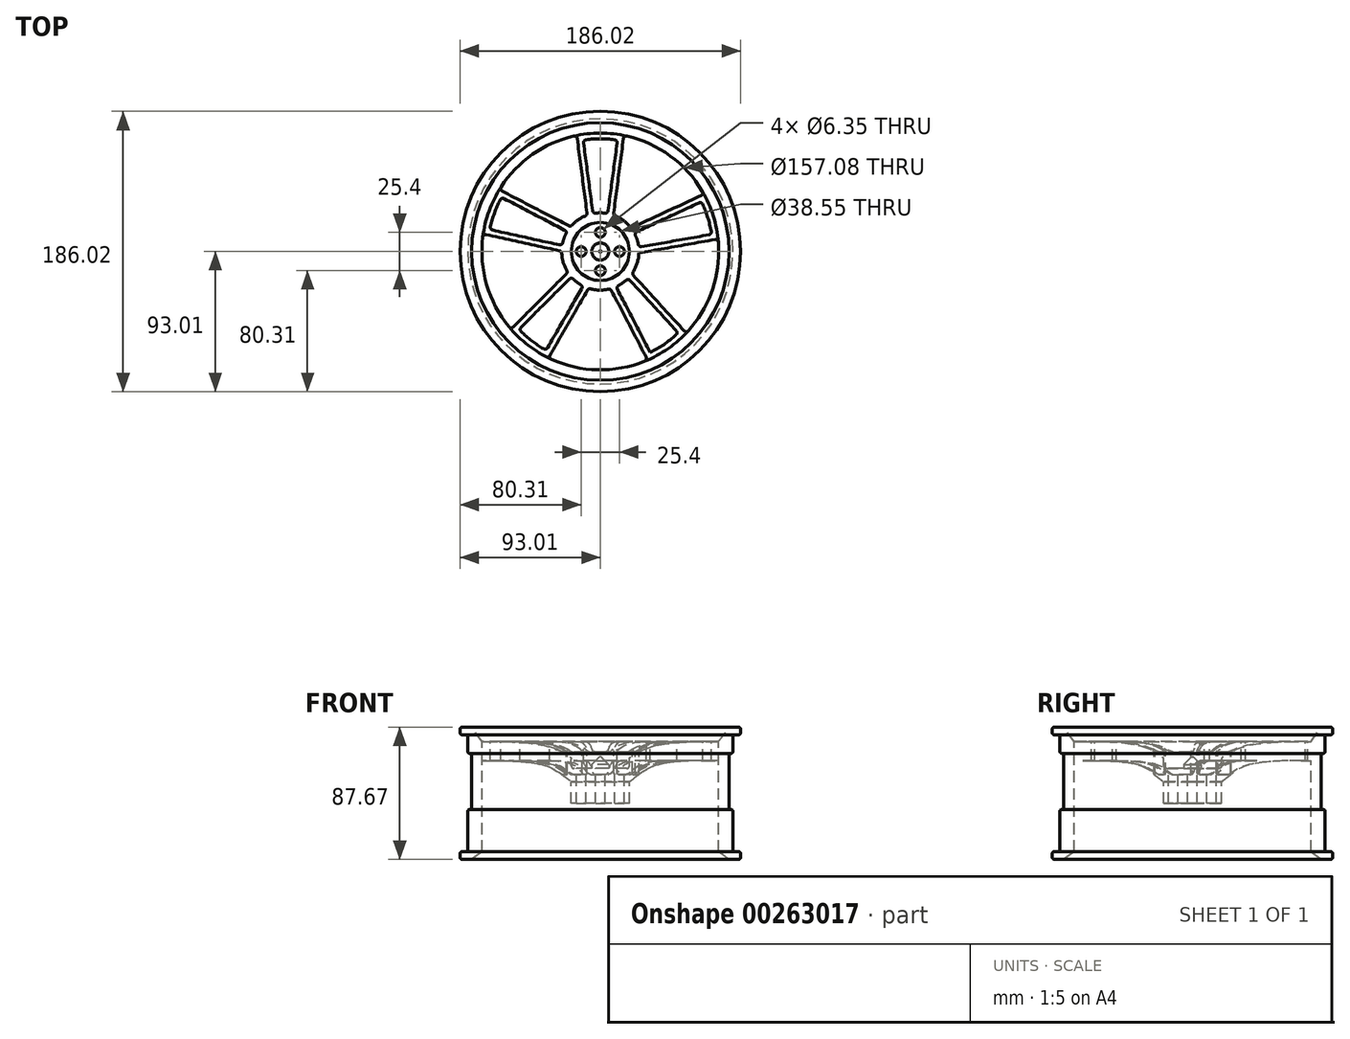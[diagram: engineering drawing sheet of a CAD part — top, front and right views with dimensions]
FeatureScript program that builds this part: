
annotation { "Feature Type Name" : "Feature", "Feature Type Description" : "" }
export const myFeature = defineFeature(function(context is Context, id is Id, definition is map)
    precondition{}
    {
        {
            var Q0;
            Q0=qCreatedBy(makeId("Front.planeOp"),FACE);
            var sketch = newSketch(context, id + "F0", { "sketchPlane" : qUnion([Q0])});
            skLineSegment(sketch, "E0", {"start": v(0, 54) * mm, "end": v(0, -73) * mm, "construction": true});
            skLineSegment(sketch, "E1", {"start": v(-93, 40.83) * mm, "end": v(-85.39, 40.83) * mm});
            skLineSegment(sketch, "E2", {"start": v(-85.39, 40.83) * mm, "end": v(-78.54, 31.34) * mm});
            skLineSegment(sketch, "E3", {"start": v(-78.54, 18.64) * mm, "end": v(-78.54, -41.76) * mm});
            skLineSegment(sketch, "E4", {"start": v(-78.54, -41.76) * mm, "end": v(-85.39, -46.84) * mm});
            skLineSegment(sketch, "E5", {"start": v(-85.39, -46.84) * mm, "end": v(-93, -46.84) * mm});
            skLineSegment(sketch, "E6", {"start": v(-93, -46.84) * mm, "end": v(-93, -41.76) * mm});
            skLineSegment(sketch, "E7", {"start": v(-93, -41.76) * mm, "end": v(-87.93, -41.76) * mm});
            skLineSegment(sketch, "E8", {"start": v(-87.93, -41.76) * mm, "end": v(-87.93, -13.7) * mm});
            skLineSegment(sketch, "E9", {"start": v(-87.93, -13.7) * mm, "end": v(-85.39, -13.7) * mm});
            skLineSegment(sketch, "E10", {"start": v(-85.39, -13.7) * mm, "end": v(-85.39, 23.42) * mm});
            skLineSegment(sketch, "E11", {"start": v(-85.39, 23.42) * mm, "end": v(-87.93, 23.42) * mm});
            skLineSegment(sketch, "E12", {"start": v(-87.93, 23.42) * mm, "end": v(-87.93, 35.75) * mm});
            skLineSegment(sketch, "E13", {"start": v(-87.93, 35.75) * mm, "end": v(-93, 35.75) * mm});
            skLineSegment(sketch, "E14", {"start": v(-93, 40.83) * mm, "end": v(-93, 35.75) * mm});
            skFitSpline(sketch, "E15", {"points": [v(-78.54, 31.34) * mm, v(-32.5, 27.25) * mm, v(-11.3, 14.38) * mm], "startDerivative": vector(88.3, -0.35) * mm, "endDerivative": vector(43.9, -35.39) * mm});
            skFitSpline(sketch, "E16.0", {"points": [v(-78.6, 18.65) * mm, v(-74.91, 18.63) * mm, v(-69.46, 18.6) * mm, v(-62.5, 18.47) * mm, v(-57.46, 18.27) * mm, v(-52.66, 17.98) * mm, v(-48.17, 17.55) * mm, v(-44.03, 16.99) * mm, v(-40.92, 16.4) * mm, v(-38.68, 15.85) * mm, v(-37.13, 15.4) * mm, v(-35.72, 14.94) * mm, v(-34.36, 14.43) * mm, v(-33.06, 13.87) * mm, v(-31.38, 13.06) * mm, v(-29.34, 11.93) * mm, v(-26.93, 10.37) * mm, v(-23.67, 8.03) * mm, v(-21.1, 5.96) * mm, v(-19.27, 4.5) * mm]});
            skLineSegment(sketch, "E17", {"start": v(-19.27, 4.5) * mm, "end": v(-19.27, -9.86) * mm});
            skLineSegment(sketch, "E18", {"start": v(-19.27, -9.86) * mm, "end": v(0, -9.86) * mm});
            skLineSegment(sketch, "E19", {"start": v(0, -9.86) * mm, "end": v(0, 13.32) * mm});
            skLineSegment(sketch, "E20", {"start": v(0, 13.32) * mm, "end": v(-19.27, 13.32) * mm});
            skLineSegment(sketch, "E21", {"start": v(-19.27, 13.32) * mm, "end": v(-19.27, 20.5) * mm});
            skSolve(sketch);
        }
        {
            var Q0;
            Q0=makeQuery(id+"F0.imprint","IMPRINT",FACE,{"disambiguationData":[TD([[makeQuery(id+"F0.imprint","IMPRINT",EDGE,{"derivedFrom":sQuery(id+"F0.wireOp",EDGE,"E1")}),-1.0]])]});
            var Q1;
            Q1=sQuery(id+"F0.wireOp",EDGE,"E0");
            revolve(context, id + "F1", {"entities" : qUnion([Q0]), "axis" : qUnion([Q1]), "revolveType" : RevolveType.FULL});
        }
        {
            var Q0;
            Q0=makeQuery(id+"F1.opRevolve","SWEPT_FACE",FACE,{"disambiguationData":[OSD([sQuery(id+"F0.wireOp",EDGE,"E1")])]});
            var sketch = newSketch(context, id + "F2", { "sketchPlane" : qUnion([Q0])});
            skArc(sketch, "E22.0", {"start": v(-77.67, 11.66) * mm, "mid": v(-75.4, -21.98) * mm, "end": v(-59.24, -51.57) * mm});
            skCircle(sketch, "E23.0", {"center": v(0, 0) * mm, "radius": 19.27 * mm});
            skArc(sketch, "E24.0", {"start": v(-25.62, 0.12) * mm, "mid": v(-24.6, -7.17) * mm, "end": v(-21.54, -13.87) * mm});
            skLineSegment(sketch, "E25", {"start": v(-8.65, 24.12) * mm, "end": v(-15.6, 76.98) * mm});
            skLineSegment(sketch, "E26", {"start": v(0, 78.54) * mm, "end": v(0, 0) * mm, "construction": true});
            skLineSegment(sketch, "E27.MirrorCS", {"start": v(8.65, 24.12) * mm, "end": v(15.6, 76.98) * mm});
            skLineSegment(sketch, "E28.1.0", {"start": v(25.6, -1) * mm, "end": v(78.1, 8.26) * mm});
            skLineSegment(sketch, "E28.1.1", {"start": v(20.4, 15.5) * mm, "end": v(68.72, 38.03) * mm});
            skLineSegment(sketch, "E28.2.0", {"start": v(6.75, -24.72) * mm, "end": v(31.37, -72) * mm});
            skLineSegment(sketch, "E28.2.1", {"start": v(20.92, -14.8) * mm, "end": v(56.93, -54.1) * mm});
            skLineSegment(sketch, "E28.3.0", {"start": v(-21.54, -13.87) * mm, "end": v(-59.24, -51.57) * mm});
            skLineSegment(sketch, "E28.3.1", {"start": v(-7.82, -24.4) * mm, "end": v(-34.48, -70.57) * mm});
            skLineSegment(sketch, "E28.4.0", {"start": v(-19.7, 16.37) * mm, "end": v(-67, 41) * mm});
            skLineSegment(sketch, "E28.4.1", {"start": v(-25.62, 0.12) * mm, "end": v(-77.67, 11.66) * mm});
            skLineSegment(sketch, "E28.anchor1", {"start": v(0, 0) * mm, "end": v(8.65, 24.12) * mm, "construction": true});
            skLineSegment(sketch, "E28.anchor2", {"start": v(0, 0) * mm, "end": v(-19.7, 16.37) * mm, "construction": true});
            skArc(sketch, "E29.trimOffspring", {"start": v(-8.65, 24.12) * mm, "mid": v(-14.7, 20.99) * mm, "end": v(-19.7, 16.37) * mm});
            skArc(sketch, "E30.trimOffspring", {"start": v(-15.6, 76.98) * mm, "mid": v(-45.05, 64.34) * mm, "end": v(-67, 41) * mm});
            skArc(sketch, "E31.trimOffspring", {"start": v(20.4, 15.5) * mm, "mid": v(15.15, 20.66) * mm, "end": v(8.65, 24.12) * mm});
            skArc(sketch, "E32.trimOffspring", {"start": v(68.72, 38.03) * mm, "mid": v(46.44, 63.34) * mm, "end": v(15.6, 76.98) * mm});
            skArc(sketch, "E33.trimOffspring", {"start": v(56.93, -54.1) * mm, "mid": v(74.37, -25.25) * mm, "end": v(78.1, 8.26) * mm});
            skArc(sketch, "E34.trimOffspring", {"start": v(20.92, -14.8) * mm, "mid": v(24.26, -8.24) * mm, "end": v(25.6, -1) * mm});
            skArc(sketch, "E35.trimOffspring", {"start": v(-7.82, -24.4) * mm, "mid": v(-0.56, -25.62) * mm, "end": v(6.75, -24.72) * mm});
            skArc(sketch, "E36.trimOffspring", {"start": v(-34.48, -70.57) * mm, "mid": v(-1.71, -78.52) * mm, "end": v(31.37, -72) * mm});
            skSolve(sketch);
        }
        {
            var Q0;
            Q0=makeQuery(id+"F1.opRevolve","SWEPT_EDGE",EDGE,{"disambiguationData":[OSD([sQuery(id+"F0.wireOp",EDGE,"E6"),sQuery(id+"F0.wireOp",EDGE,"E7")])]});
            var Q1;
            Q1=makeQuery(id+"F1.opRevolve","SWEPT_FACE",FACE,{"disambiguationData":[OSD([sQuery(id+"F0.wireOp",EDGE,"E10")])]});
            var Q2;
            Q2=makeQuery(id+"F1.opRevolve","SWEPT_EDGE",EDGE,{"disambiguationData":[OSD([sQuery(id+"F0.wireOp",EDGE,"E8"),sQuery(id+"F0.wireOp",EDGE,"E9")])]});
            var Q3;
            Q3=makeQuery(id+"F1.opRevolve","SWEPT_EDGE",EDGE,{"disambiguationData":[OSD([sQuery(id+"F0.wireOp",EDGE,"E11"),sQuery(id+"F0.wireOp",EDGE,"E12")])]});
            var Q4;
            Q4=makeQuery(id+"F1.opRevolve","SWEPT_EDGE",EDGE,{"disambiguationData":[OSD([sQuery(id+"F0.wireOp",EDGE,"E13"),sQuery(id+"F0.wireOp",EDGE,"E14")])]});
            var Q5;
            Q5=makeQuery(id+"F1.opRevolve","SWEPT_EDGE",EDGE,{"disambiguationData":[OSD([sQuery(id+"F0.wireOp",EDGE,"E12"),sQuery(id+"F0.wireOp",EDGE,"E13")])]});
            var Q6;
            Q6=makeQuery(id+"F1.opRevolve","SWEPT_EDGE",EDGE,{"disambiguationData":[OSD([sQuery(id+"F0.wireOp",EDGE,"E1"),sQuery(id+"F0.wireOp",EDGE,"E14")])]});
            var Q7;
            Q7=makeQuery(id+"F1.opRevolve","SWEPT_EDGE",EDGE,{"disambiguationData":[OSD([sQuery(id+"F0.wireOp",EDGE,"E5"),sQuery(id+"F0.wireOp",EDGE,"E6")])]});
            fillet(context, id + "F3", {"entities" : qUnion([Q0, Q1, Q2, Q3, Q4, Q5, Q6, Q7]), "radius" : 1.27 * mm, "tangentPropagation" : true, "allowEdgeOverflow" : false});
        }
        {
            var Q0;
            Q0=makeQuery(id+"F2.imprint","IMPRINT",FACE,{"disambiguationData":[TD([[makeQuery(id+"F2.imprint","IMPRINT",EDGE,{"derivedFrom":sQuery(id+"F2.wireOp",EDGE,"E28.1.0")}),-1.0]])]});
            var Q1;
            Q1=makeQuery(id+"F2.imprint","IMPRINT",FACE,{"disambiguationData":[TD([[makeQuery(id+"F2.imprint","IMPRINT",EDGE,{"derivedFrom":sQuery(id+"F2.wireOp",EDGE,"E27.MirrorCS")}),-1.0]])]});
            var Q2;
            Q2=makeQuery(id+"F2.imprint","IMPRINT",FACE,{"disambiguationData":[TD([[makeQuery(id+"F2.imprint","IMPRINT",EDGE,{"derivedFrom":sQuery(id+"F2.wireOp",EDGE,"E25")}),1.0]])]});
            var Q3;
            Q3=makeQuery(id+"F2.imprint","IMPRINT",FACE,{"disambiguationData":[TD([[makeQuery(id+"F2.imprint","IMPRINT",EDGE,{"derivedFrom":sQuery(id+"F2.wireOp",EDGE,"E22.0")}),1.0]])]});
            var Q4;
            Q4=makeQuery(id+"F2.imprint","IMPRINT",FACE,{"disambiguationData":[TD([[makeQuery(id+"F2.imprint","IMPRINT",EDGE,{"derivedFrom":sQuery(id+"F2.wireOp",EDGE,"E28.2.0")}),-1.0]])]});
            extrude(context, id + "F4", {"entities" : qUnion([Q0, Q1, Q2, Q3, Q4]), "operationType" : NewBodyOperationType.REMOVE, "oppositeDirection" : true, "depth" : 127 * mm});
        }
        {
            var Q0;
            Q0=makeQuery(id+"F1.opRevolve","SWEPT_FACE",FACE,{"disambiguationData":[OSD([sQuery(id+"F0.wireOp",EDGE,"E1")])]});
            var sketch = newSketch(context, id + "F5", { "sketchPlane" : qUnion([Q0])});
            skArc(sketch, "E37.0", {"start": v(11.35, 73.87) * mm, "mid": v(0, 74.73) * mm, "end": v(-11.35, 73.87) * mm});
            skPoint(sketch, "E38.2.end.orphan", {"position": v(8.65, 24.12) * mm});
            skPoint(sketch, "E38.2.start.orphan", {"position": v(15.6, 76.98) * mm});
            skPoint(sketch, "E38.1.end.orphan", {"position": v(-8.65, 24.12) * mm});
            skPoint(sketch, "E38.1.start.orphan", {"position": v(-15.6, 76.98) * mm});
            skArc(sketch, "E39", {"start": v(4.94, 25.14) * mm, "mid": v(0, 25.62) * mm, "end": v(-4.94, 25.14) * mm});
            skLineSegment(sketch, "E40", {"start": v(-11.35, 73.87) * mm, "end": v(-4.94, 25.14) * mm});
            skLineSegment(sketch, "E41", {"start": v(11.35, 73.87) * mm, "end": v(4.94, 25.14) * mm});
            skArc(sketch, "E42.1.0", {"start": v(73.86, 11.38) * mm, "mid": v(71.27, 22.47) * mm, "end": v(67.03, 33.04) * mm});
            skLineSegment(sketch, "E42.1.1", {"start": v(73.86, 11.38) * mm, "end": v(25.46, 2.85) * mm});
            skArc(sketch, "E42.1.2", {"start": v(25.46, 2.85) * mm, "mid": v(24.44, 7.7) * mm, "end": v(22.5, 12.27) * mm});
            skLineSegment(sketch, "E42.1.3", {"start": v(67.03, 33.04) * mm, "end": v(22.5, 12.27) * mm});
            skArc(sketch, "E42.2.0", {"start": v(33.07, -67.02) * mm, "mid": v(42.86, -61.22) * mm, "end": v(51.67, -54) * mm});
            skLineSegment(sketch, "E42.2.1", {"start": v(33.07, -67.02) * mm, "end": v(10.38, -23.43) * mm});
            skArc(sketch, "E42.2.2", {"start": v(10.38, -23.43) * mm, "mid": v(14.7, -20.99) * mm, "end": v(18.47, -17.76) * mm});
            skLineSegment(sketch, "E42.2.3", {"start": v(51.67, -54) * mm, "end": v(18.47, -17.76) * mm});
            skArc(sketch, "E42.3.0", {"start": v(-53.97, -51.7) * mm, "mid": v(-45.5, -59.29) * mm, "end": v(-35.96, -65.51) * mm});
            skLineSegment(sketch, "E42.3.1", {"start": v(-53.97, -51.7) * mm, "end": v(-19.22, -16.94) * mm});
            skArc(sketch, "E42.3.2", {"start": v(-19.22, -16.94) * mm, "mid": v(-15.6, -20.33) * mm, "end": v(-11.39, -22.95) * mm});
            skLineSegment(sketch, "E42.3.3", {"start": v(-35.96, -65.51) * mm, "end": v(-11.39, -22.95) * mm});
            skArc(sketch, "E42.4.0", {"start": v(-65.53, 35.93) * mm, "mid": v(-70.23, 25.56) * mm, "end": v(-73.3, 14.6) * mm});
            skLineSegment(sketch, "E42.4.1", {"start": v(-65.53, 35.93) * mm, "end": v(-21.94, 13.24) * mm});
            skArc(sketch, "E42.4.2", {"start": v(-21.94, 13.24) * mm, "mid": v(-24.08, 8.76) * mm, "end": v(-25.32, 3.96) * mm});
            skLineSegment(sketch, "E42.4.3", {"start": v(-73.3, 14.6) * mm, "end": v(-25.32, 3.96) * mm});
            skLineSegment(sketch, "E42.anchor1", {"start": v(0, 0) * mm, "end": v(-4.94, 25.14) * mm, "construction": true});
            skLineSegment(sketch, "E42.anchor2", {"start": v(0, 0) * mm, "end": v(-25.32, 3.96) * mm, "construction": true});
            skSolve(sketch);
        }
        {
            var Q0;
            Q0 = qSketchRegion(id + "F5", true);
            var Q1;
            Q1=makeQuery(id+"F1.opRevolve","SWEPT_FACE",FACE,{"disambiguationData":[OSD([sQuery(id+"F0.wireOp",EDGE,"E16.0")])]});
            extrude(context, id + "F6", {"entities" : qUnion([Q0]), "operationType" : NewBodyOperationType.REMOVE, "endBound" : BoundingType.UP_TO_SURFACE, "oppositeDirection" : true, "endBoundEntityFace" : qUnion([Q1]), "depth" : 25.4 * mm});
        }
        {
            var Q0;
            Q0=makeQuery(id+"F6.boolean.opBoolean","COPY",EDGE,{"derivedFrom":makeQuery(id+"F6.opExtrude","SWEPT_EDGE",EDGE,{"disambiguationData":[OSD([sQuery(id+"F5.wireOp",EDGE,"E37.0"),sQuery(id+"F5.wireOp",EDGE,"E40")])]})});
            var Q1;
            Q1=makeQuery(id+"F6.boolean.opBoolean","COPY",EDGE,{"derivedFrom":makeQuery(id+"F6.opExtrude","SWEPT_EDGE",EDGE,{"disambiguationData":[OSD([sQuery(id+"F5.wireOp",EDGE,"E37.0"),sQuery(id+"F5.wireOp",EDGE,"E41")])]})});
            var Q2;
            Q2=makeQuery(id+"F6.boolean.opBoolean","COPY",EDGE,{"derivedFrom":makeQuery(id+"F6.opExtrude","SWEPT_EDGE",EDGE,{"disambiguationData":[OSD([sQuery(id+"F5.wireOp",EDGE,"E42.1.0"),sQuery(id+"F5.wireOp",EDGE,"E42.1.3")])]})});
            var Q3;
            Q3=makeQuery(id+"F4.boolean.opBoolean","COPY",EDGE,{"derivedFrom":makeQuery(id+"F4.opExtrude","SWEPT_EDGE",EDGE,{"disambiguationData":[OSD([sQuery(id+"F2.wireOp",EDGE,"E27.MirrorCS"),sQuery(id+"F2.wireOp",EDGE,"E32.trimOffspring")])]})});
            var Q4;
            Q4=makeQuery(id+"F4.boolean.opBoolean","COPY",EDGE,{"derivedFrom":makeQuery(id+"F4.opExtrude","SWEPT_EDGE",EDGE,{"disambiguationData":[OSD([sQuery(id+"F2.wireOp",EDGE,"E25"),sQuery(id+"F2.wireOp",EDGE,"E30.trimOffspring")])]})});
            var Q5;
            Q5=makeQuery(id+"F6.boolean.opBoolean","COPY",EDGE,{"derivedFrom":makeQuery(id+"F6.opExtrude","SWEPT_EDGE",EDGE,{"disambiguationData":[OSD([sQuery(id+"F5.wireOp",EDGE,"E42.1.0"),sQuery(id+"F5.wireOp",EDGE,"E42.1.1")])]})});
            var Q6;
            Q6=makeQuery(id+"F4.boolean.opBoolean","COPY",EDGE,{"derivedFrom":makeQuery(id+"F4.opExtrude","SWEPT_EDGE",EDGE,{"disambiguationData":[OSD([sQuery(id+"F2.wireOp",EDGE,"E28.1.0"),sQuery(id+"F2.wireOp",EDGE,"E33.trimOffspring")])]})});
            var Q7;
            Q7=makeQuery(id+"F4.boolean.opBoolean","COPY",EDGE,{"derivedFrom":makeQuery(id+"F4.opExtrude","SWEPT_EDGE",EDGE,{"disambiguationData":[OSD([sQuery(id+"F2.wireOp",EDGE,"E28.1.1"),sQuery(id+"F2.wireOp",EDGE,"E32.trimOffspring")])]})});
            var Q8;
            Q8=makeQuery(id+"F4.boolean.opBoolean","COPY",EDGE,{"derivedFrom":makeQuery(id+"F4.opExtrude","SWEPT_EDGE",EDGE,{"disambiguationData":[OSD([sQuery(id+"F2.wireOp",EDGE,"E28.2.0"),sQuery(id+"F2.wireOp",EDGE,"E36.trimOffspring")])]})});
            var Q9;
            Q9=makeQuery(id+"F6.boolean.opBoolean","COPY",EDGE,{"derivedFrom":makeQuery(id+"F6.opExtrude","SWEPT_EDGE",EDGE,{"disambiguationData":[OSD([sQuery(id+"F5.wireOp",EDGE,"E42.2.0"),sQuery(id+"F5.wireOp",EDGE,"E42.2.3")])]})});
            var Q10;
            Q10=makeQuery(id+"F4.boolean.opBoolean","COPY",EDGE,{"derivedFrom":makeQuery(id+"F4.opExtrude","SWEPT_EDGE",EDGE,{"disambiguationData":[OSD([sQuery(id+"F2.wireOp",EDGE,"E28.2.1"),sQuery(id+"F2.wireOp",EDGE,"E33.trimOffspring")])]})});
            var Q11;
            Q11=makeQuery(id+"F4.boolean.opBoolean","COPY",EDGE,{"derivedFrom":makeQuery(id+"F4.opExtrude","SWEPT_EDGE",EDGE,{"disambiguationData":[OSD([sQuery(id+"F2.wireOp",EDGE,"E28.3.1"),sQuery(id+"F2.wireOp",EDGE,"E36.trimOffspring")])]})});
            var Q12;
            Q12=makeQuery(id+"F6.boolean.opBoolean","COPY",EDGE,{"derivedFrom":makeQuery(id+"F6.opExtrude","SWEPT_EDGE",EDGE,{"disambiguationData":[OSD([sQuery(id+"F5.wireOp",EDGE,"E42.3.0"),sQuery(id+"F5.wireOp",EDGE,"E42.3.1")])]})});
            var Q13;
            Q13=makeQuery(id+"F6.boolean.opBoolean","COPY",EDGE,{"derivedFrom":makeQuery(id+"F6.opExtrude","SWEPT_EDGE",EDGE,{"disambiguationData":[OSD([sQuery(id+"F5.wireOp",EDGE,"E42.3.0"),sQuery(id+"F5.wireOp",EDGE,"E42.3.3")])]})});
            var Q14;
            Q14=makeQuery(id+"F4.boolean.opBoolean","COPY",EDGE,{"derivedFrom":makeQuery(id+"F4.opExtrude","SWEPT_EDGE",EDGE,{"disambiguationData":[OSD([sQuery(id+"F2.wireOp",EDGE,"E22.0"),sQuery(id+"F2.wireOp",EDGE,"E28.3.0")])]})});
            var Q15;
            Q15=makeQuery(id+"F4.boolean.opBoolean","COPY",EDGE,{"derivedFrom":makeQuery(id+"F4.opExtrude","SWEPT_EDGE",EDGE,{"disambiguationData":[OSD([sQuery(id+"F2.wireOp",EDGE,"E22.0"),sQuery(id+"F2.wireOp",EDGE,"E28.4.1")])]})});
            var Q16;
            Q16=makeQuery(id+"F6.boolean.opBoolean","COPY",EDGE,{"derivedFrom":makeQuery(id+"F6.opExtrude","SWEPT_EDGE",EDGE,{"disambiguationData":[OSD([sQuery(id+"F5.wireOp",EDGE,"E42.4.0"),sQuery(id+"F5.wireOp",EDGE,"E42.4.1")])]})});
            var Q17;
            Q17=makeQuery(id+"F4.boolean.opBoolean","COPY",EDGE,{"derivedFrom":makeQuery(id+"F4.opExtrude","SWEPT_EDGE",EDGE,{"disambiguationData":[OSD([sQuery(id+"F2.wireOp",EDGE,"E28.4.0"),sQuery(id+"F2.wireOp",EDGE,"E30.trimOffspring")])]})});
            var Q18;
            Q18=makeQuery(id+"F6.boolean.opBoolean","COPY",EDGE,{"derivedFrom":makeQuery(id+"F6.opExtrude","SWEPT_EDGE",EDGE,{"disambiguationData":[OSD([sQuery(id+"F5.wireOp",EDGE,"E42.4.0"),sQuery(id+"F5.wireOp",EDGE,"E42.4.3")])]})});
            var Q19;
            Q19=makeQuery(id+"F4.boolean.opBoolean","COPY",EDGE,{"derivedFrom":makeQuery(id+"F4.opExtrude","SWEPT_EDGE",EDGE,{"disambiguationData":[OSD([sQuery(id+"F2.wireOp",EDGE,"E27.MirrorCS"),sQuery(id+"F2.wireOp",EDGE,"E31.trimOffspring")])]})});
            var Q20;
            Q20=makeQuery(id+"F4.boolean.opBoolean","COPY",EDGE,{"derivedFrom":makeQuery(id+"F4.opExtrude","SWEPT_EDGE",EDGE,{"disambiguationData":[OSD([sQuery(id+"F2.wireOp",EDGE,"E28.1.1"),sQuery(id+"F2.wireOp",EDGE,"E31.trimOffspring")])]})});
            var Q21;
            Q21=makeQuery(id+"F6.boolean.opBoolean","COPY",EDGE,{"derivedFrom":makeQuery(id+"F6.opExtrude","SWEPT_EDGE",EDGE,{"disambiguationData":[OSD([sQuery(id+"F5.wireOp",EDGE,"E39"),sQuery(id+"F5.wireOp",EDGE,"E41")])]})});
            var Q22;
            Q22=makeQuery(id+"F6.boolean.opBoolean","COPY",EDGE,{"derivedFrom":makeQuery(id+"F6.opExtrude","SWEPT_EDGE",EDGE,{"disambiguationData":[OSD([sQuery(id+"F5.wireOp",EDGE,"E39"),sQuery(id+"F5.wireOp",EDGE,"E40")])]})});
            var Q23;
            Q23=makeQuery(id+"F4.boolean.opBoolean","COPY",EDGE,{"derivedFrom":makeQuery(id+"F4.opExtrude","SWEPT_EDGE",EDGE,{"disambiguationData":[OSD([sQuery(id+"F2.wireOp",EDGE,"E25"),sQuery(id+"F2.wireOp",EDGE,"E29.trimOffspring")])]})});
            var Q24;
            Q24=makeQuery(id+"F4.boolean.opBoolean","COPY",EDGE,{"derivedFrom":makeQuery(id+"F4.opExtrude","SWEPT_EDGE",EDGE,{"disambiguationData":[OSD([sQuery(id+"F2.wireOp",EDGE,"E28.4.0"),sQuery(id+"F2.wireOp",EDGE,"E29.trimOffspring")])]})});
            var Q25;
            Q25=makeQuery(id+"F6.boolean.opBoolean","COPY",EDGE,{"derivedFrom":makeQuery(id+"F6.opExtrude","SWEPT_EDGE",EDGE,{"disambiguationData":[OSD([sQuery(id+"F5.wireOp",EDGE,"E42.4.1"),sQuery(id+"F5.wireOp",EDGE,"E42.4.2")])]})});
            var Q26;
            Q26=makeQuery(id+"F6.boolean.opBoolean","COPY",EDGE,{"derivedFrom":makeQuery(id+"F6.opExtrude","SWEPT_EDGE",EDGE,{"disambiguationData":[OSD([sQuery(id+"F5.wireOp",EDGE,"E42.4.2"),sQuery(id+"F5.wireOp",EDGE,"E42.4.3")])]})});
            var Q27;
            Q27=makeQuery(id+"F4.boolean.opBoolean","COPY",EDGE,{"derivedFrom":makeQuery(id+"F4.opExtrude","SWEPT_EDGE",EDGE,{"disambiguationData":[OSD([sQuery(id+"F2.wireOp",EDGE,"E24.0"),sQuery(id+"F2.wireOp",EDGE,"E28.4.1")])]})});
            var Q28;
            Q28=makeQuery(id+"F4.boolean.opBoolean","COPY",EDGE,{"derivedFrom":makeQuery(id+"F4.opExtrude","SWEPT_EDGE",EDGE,{"disambiguationData":[OSD([sQuery(id+"F2.wireOp",EDGE,"E24.0"),sQuery(id+"F2.wireOp",EDGE,"E28.3.0")])]})});
            var Q29;
            Q29=makeQuery(id+"F6.boolean.opBoolean","COPY",EDGE,{"derivedFrom":makeQuery(id+"F6.opExtrude","SWEPT_EDGE",EDGE,{"disambiguationData":[OSD([sQuery(id+"F5.wireOp",EDGE,"E42.3.1"),sQuery(id+"F5.wireOp",EDGE,"E42.3.2")])]})});
            var Q30;
            Q30=makeQuery(id+"F6.boolean.opBoolean","COPY",EDGE,{"derivedFrom":makeQuery(id+"F6.opExtrude","SWEPT_EDGE",EDGE,{"disambiguationData":[OSD([sQuery(id+"F5.wireOp",EDGE,"E42.3.2"),sQuery(id+"F5.wireOp",EDGE,"E42.3.3")])]})});
            var Q31;
            Q31=makeQuery(id+"F4.boolean.opBoolean","COPY",EDGE,{"derivedFrom":makeQuery(id+"F4.opExtrude","SWEPT_EDGE",EDGE,{"disambiguationData":[OSD([sQuery(id+"F2.wireOp",EDGE,"E28.3.1"),sQuery(id+"F2.wireOp",EDGE,"E35.trimOffspring")])]})});
            var Q32;
            Q32=makeQuery(id+"F4.boolean.opBoolean","COPY",EDGE,{"derivedFrom":makeQuery(id+"F4.opExtrude","SWEPT_EDGE",EDGE,{"disambiguationData":[OSD([sQuery(id+"F2.wireOp",EDGE,"E28.2.0"),sQuery(id+"F2.wireOp",EDGE,"E35.trimOffspring")])]})});
            var Q33;
            Q33=makeQuery(id+"F6.boolean.opBoolean","COPY",EDGE,{"derivedFrom":makeQuery(id+"F6.opExtrude","SWEPT_EDGE",EDGE,{"disambiguationData":[OSD([sQuery(id+"F5.wireOp",EDGE,"E42.2.1"),sQuery(id+"F5.wireOp",EDGE,"E42.2.2")])]})});
            var Q34;
            Q34=makeQuery(id+"F4.boolean.opBoolean","COPY",EDGE,{"derivedFrom":makeQuery(id+"F4.opExtrude","SWEPT_EDGE",EDGE,{"disambiguationData":[OSD([sQuery(id+"F2.wireOp",EDGE,"E28.2.1"),sQuery(id+"F2.wireOp",EDGE,"E34.trimOffspring")])]})});
            var Q35;
            Q35=makeQuery(id+"F6.boolean.opBoolean","COPY",EDGE,{"derivedFrom":makeQuery(id+"F6.opExtrude","SWEPT_EDGE",EDGE,{"disambiguationData":[OSD([sQuery(id+"F5.wireOp",EDGE,"E42.1.1"),sQuery(id+"F5.wireOp",EDGE,"E42.1.2")])]})});
            var Q36;
            Q36=makeQuery(id+"F6.boolean.opBoolean","COPY",EDGE,{"derivedFrom":makeQuery(id+"F6.opExtrude","SWEPT_EDGE",EDGE,{"disambiguationData":[OSD([sQuery(id+"F5.wireOp",EDGE,"E42.2.2"),sQuery(id+"F5.wireOp",EDGE,"E42.2.3")])]})});
            var Q37;
            Q37=makeQuery(id+"F6.boolean.opBoolean","COPY",EDGE,{"derivedFrom":makeQuery(id+"F6.opExtrude","SWEPT_EDGE",EDGE,{"disambiguationData":[OSD([sQuery(id+"F5.wireOp",EDGE,"E42.1.2"),sQuery(id+"F5.wireOp",EDGE,"E42.1.3")])]})});
            var Q38;
            Q38=makeQuery(id+"F1.opRevolve","SWEPT_EDGE",EDGE,{"disambiguationData":[OSD([sQuery(id+"F0.wireOp",EDGE,"E20"),sQuery(id+"F0.wireOp",EDGE,"E21")])]});
            var Q39;
            Q39=makeQuery(id+"F1.opRevolve","SWEPT_EDGE",EDGE,{"disambiguationData":[OSD([sQuery(id+"F0.wireOp",EDGE,"E15"),sQuery(id+"F0.wireOp",EDGE,"E21")])]});
            fillet(context, id + "F7", {"entities" : qUnion([Q0, Q1, Q2, Q3, Q4, Q5, Q6, Q7, Q8, Q9, Q10, Q11, Q12, Q13, Q14, Q15, Q16, Q17, Q18, Q19, Q20, Q21, Q22, Q23, Q24, Q25, Q26, Q27, Q28, Q29, Q30, Q31, Q32, Q33, Q34, Q35, Q36, Q37, Q38, Q39]), "radius" : 1.9 * mm, "tangentPropagation" : true, "allowEdgeOverflow" : false});
        }
        {
            var Q0;
            Q0=makeQuery(id+"F1.opRevolve","SWEPT_FACE",FACE,{"disambiguationData":[OSD([sQuery(id+"F0.wireOp",EDGE,"E20")])]});
            var sketch = newSketch(context, id + "F8", { "sketchPlane" : qUnion([Q0])});
            skCircle(sketch, "E43", {"center": v(0, 12.7) * mm, "radius": 2.54 * mm});
            skCircle(sketch, "E44.1.0", {"center": v(-12.7, 0) * mm, "radius": 2.54 * mm});
            skCircle(sketch, "E44.2.0", {"center": v(0, -12.7) * mm, "radius": 2.54 * mm});
            skCircle(sketch, "E44.3.0", {"center": v(12.7, 0) * mm, "radius": 2.54 * mm});
            skPoint(sketch, "E44.center", {"position": v(0, 0) * mm});
            skSolve(sketch);
        }
        {
            var Q0;
            Q0=sQuery(id+"F8.wireOp",VERTEX,"E43.center");
            var Q1;
            Q1=sQuery(id+"F8.wireOp",VERTEX,"E44.3.0.center");
            var Q2;
            Q2=sQuery(id+"F8.wireOp",VERTEX,"E44.2.0.center");
            var Q3;
            Q3=sQuery(id+"F8.wireOp",VERTEX,"E44.1.0.center");
            var Q4;
            Q4=makeQuery(id+"F1.opRevolve","SWEPT_BODY",BODY,{"disambiguationData":[OSD([sQuery(id+"F0.wireOp",EDGE,"E1"),sQuery(id+"F0.wireOp",EDGE,"E2"),sQuery(id+"F0.wireOp",EDGE,"E3"),sQuery(id+"F0.wireOp",EDGE,"E4"),sQuery(id+"F0.wireOp",EDGE,"E5"),sQuery(id+"F0.wireOp",EDGE,"E6"),sQuery(id+"F0.wireOp",EDGE,"E7"),sQuery(id+"F0.wireOp",EDGE,"E8"),sQuery(id+"F0.wireOp",EDGE,"E9"),sQuery(id+"F0.wireOp",EDGE,"E10"),sQuery(id+"F0.wireOp",EDGE,"E11"),sQuery(id+"F0.wireOp",EDGE,"E12"),sQuery(id+"F0.wireOp",EDGE,"E13"),sQuery(id+"F0.wireOp",EDGE,"E14"),sQuery(id+"F0.wireOp",EDGE,"E15"),sQuery(id+"F0.wireOp",EDGE,"E16.0"),sQuery(id+"F0.wireOp",EDGE,"E17"),sQuery(id+"F0.wireOp",EDGE,"E18"),sQuery(id+"F0.wireOp",EDGE,"E19"),sQuery(id+"F0.wireOp",EDGE,"E20"),sQuery(id+"F0.wireOp",EDGE,"E21")])]});
            hole(context, id + "F9", {"style" : HoleStyle.SIMPLE, "endStyle" : HoleEndStyle.THROUGH, "holeDiameter" : 6.35 * mm, "tappedDepth" : 12.7 * mm, "tapClearance" : 3, "locations" : qUnion([Q0, Q1, Q2, Q3]), "scope" : qUnion([Q4])});
        }
        {
            var Q0;
            Q0=makeQuery(id+"F1.opRevolve","SWEPT_FACE",FACE,{"disambiguationData":[OSD([sQuery(id+"F0.wireOp",EDGE,"E20")])]});
            var sketch = newSketch(context, id + "F10", { "sketchPlane" : qUnion([Q0])});
            skCircle(sketch, "E45", {"center": v(0, 0) * mm, "radius": 5.68 * mm});
            skSolve(sketch);
        }
        {
            var Q0;
            Q0 = qSketchRegion(id + "F10", true);
            extrude(context, id + "F11", {"entities" : qUnion([Q0]), "operationType" : NewBodyOperationType.ADD, "depth" : 7.62 * mm});
        }
        {
            var Q0;
            Q0=makeQuery(id+"F11.opExtrude","CAP_FACE",FACE,{"disambiguationData":[OSD([sQuery(id+"F10.wireOp",EDGE,"E45")])],"isStart":false});
            chamfer(context, id + "F12", {"entities" : qUnion([Q0]), "width" : 5.08 * mm, "tangentPropagation" : true});
        }
    });
